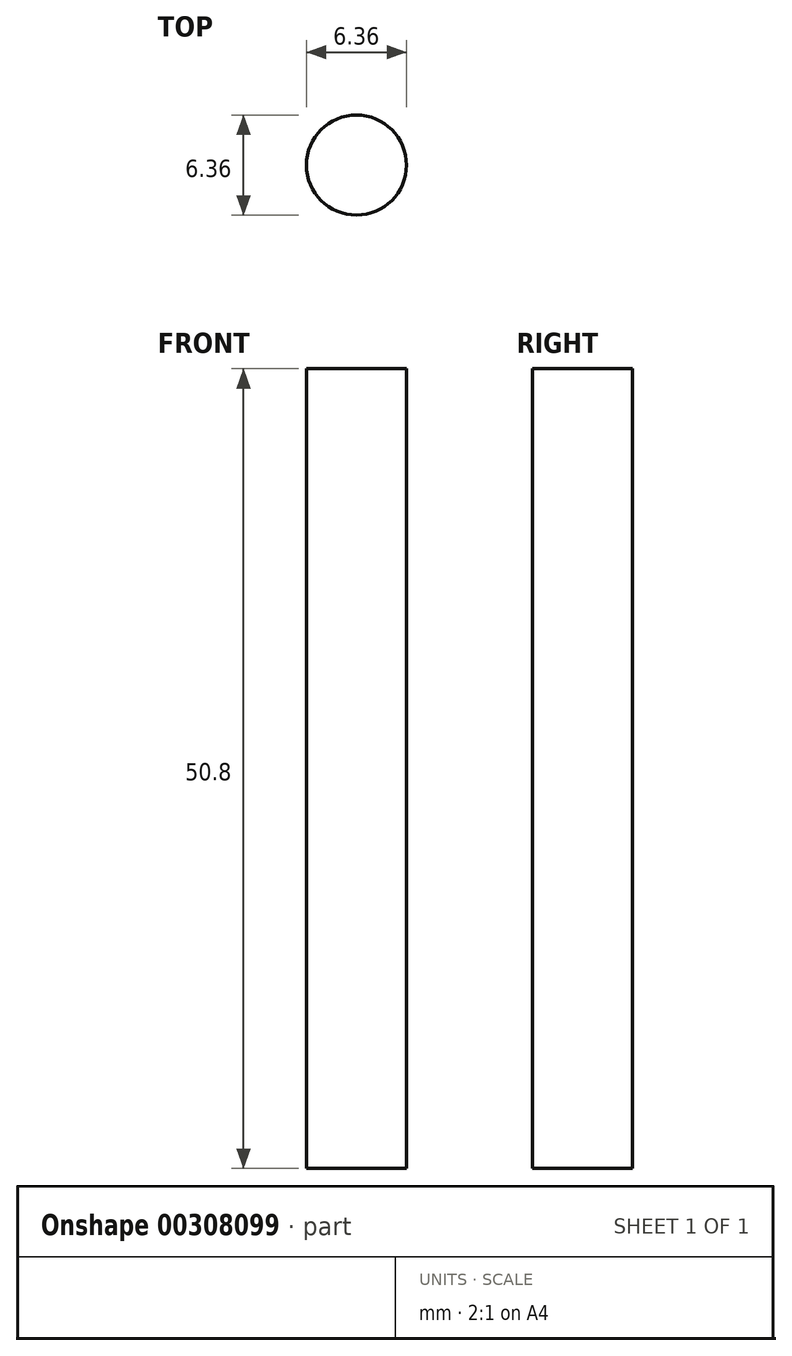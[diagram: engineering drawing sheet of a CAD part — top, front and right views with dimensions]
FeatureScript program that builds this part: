
annotation { "Feature Type Name" : "Feature", "Feature Type Description" : "" }
export const myFeature = defineFeature(function(context is Context, id is Id, definition is map)
    precondition{}
    {
        {
            var Q0;
            Q0=qCreatedBy(makeId("Top.planeOp"),FACE);
            var sketch = newSketch(context, id + "F0", { "sketchPlane" : qUnion([Q0])});
            skCircle(sketch, "E0", {"center": v(0, 0) * mm, "radius": 3.17 * mm});
            skSolve(sketch);
        }
        {
            var Q0;
            Q0 = qSketchRegion(id + "F0", true);
            extrude(context, id + "F1", {"entities" : qUnion([Q0]), "depth" : 50.8 * mm});
        }
    });
